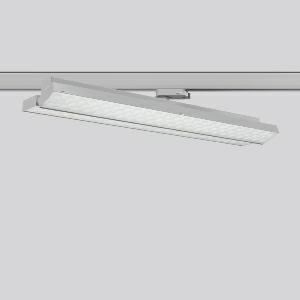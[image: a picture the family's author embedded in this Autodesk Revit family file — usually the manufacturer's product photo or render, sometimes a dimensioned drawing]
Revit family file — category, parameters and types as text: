
# Revit family: tx-move_742162_004_3_4fe9
name_source: partatom
category: Lighting Fixtures
units: mm (PartAtom-declared; Revit-internal decimal feet)

## family parameters
Cut with Voids When Loaded = No
Host = Face
Light Source = No
Part Type = Normal
Room Calculation Point = No
Round Connector Dimension = Use Diameter
Shared = No

## types (1)
- MultiLumen 1 (1 x LED Modul 835, 3050 lm, 3500)
    Apparent Load = 41 VA
    CIE Flux Codes = 77 96 99 100 100
    Color Rendering = 80
    Color Temperature = 3500
    Default Elevation = 1800 mm
    Description = Series: TX-MOVE
Multifunctional surface-mounted spotlight for area lighting. Very flat design. Housing: sheet steel, powder-coated. Rotation range: 356°. Swivel range: 90°. Consistent alignment possible with visible tilt scale. High-efficiency LED units with optimum light control thanks to clear plastic (PC) lens optics. Spezielle Mikrostrukturen reduzieren Gelbsaum. Symmetrical light distribution. With multi adaptor for 3-circuit tracks 230 V. Suitable for Track on ceiling. MultiLumen: Luminous flux adjustable in 3 steps. Factory setting is the highest luminous flux. Environmentally friendly and resource-saving due to replaceable and recyclable components. 
Colour: silver, matt (approx. RAL 9006)
Length: 570 mm
Width: 119 mm
Height: 92 mm
Lamp: LED
Socket: without socket
Colour temperature: 3500K
Colour rendering index (CRI): 80
System power: 41 W
Rated luminous flux: 6100 lm
Luminous efficiency: 149 lm/W
System power 2: 57 W
Rated luminous flux 2: 8300 lm
Luminous efficiency 2: 146 lm/W
System power 3: 73 W
Rated luminous flux 3: 10200 lm
Luminous efficiency 3: 140 lm/W
Control gear: Regulated power supply
Protection class: I
Type of protection: IP 20
    Height = 75 mm
    Lamp = 1 x LED Modul 835
    Lamp Light Flux = 3050 lm
    Lamp count = 1
    Length = 569 mm
    Lifetime = 50000 h
    Luminous efficacy = 149 lm/W
    Manufacturer = RZB
    ModVariant = No
    Model = 742162.004.3
    Mounting Place = Ceiling
    Mounting Type = Rail mounted
    Number of Poles = 1
    OnlyDefault = Yes
    Power Factor = 1
    Product Name = TX-MOVE
    Product group = Track mounted projectors
    ProductGroupID = 301
    Protection Class = Protection class I
    Protection Degree = IP 20
    RLX_Detail_Level = 1
    RLX_Emergency_Light_Flux = 0 lm
    RLX_Emergency_Type = 0
    RLX_Emergency_Type_DB = No
    RlxData = <blob elided: 33197 chars, md5=e924e64e>
    Socket = socket
    Standby Power = 0 W
    System Light Flux = 6100 lm
    System Power = 41 W
    Type Comments = MultiLumen 1
    Type Image = 742162.004.jpg
    URL = http://relux.com
    VarID = multilumen_1
    Voltage = 230 V
    Voltage Range = 220-240 V
    Weight = 0.00 kg
    Width = 119 mm

## geometry (parser evidence)
native form markers: Blend x4, Sweep x15
no freeform markers — native parametric forms only
